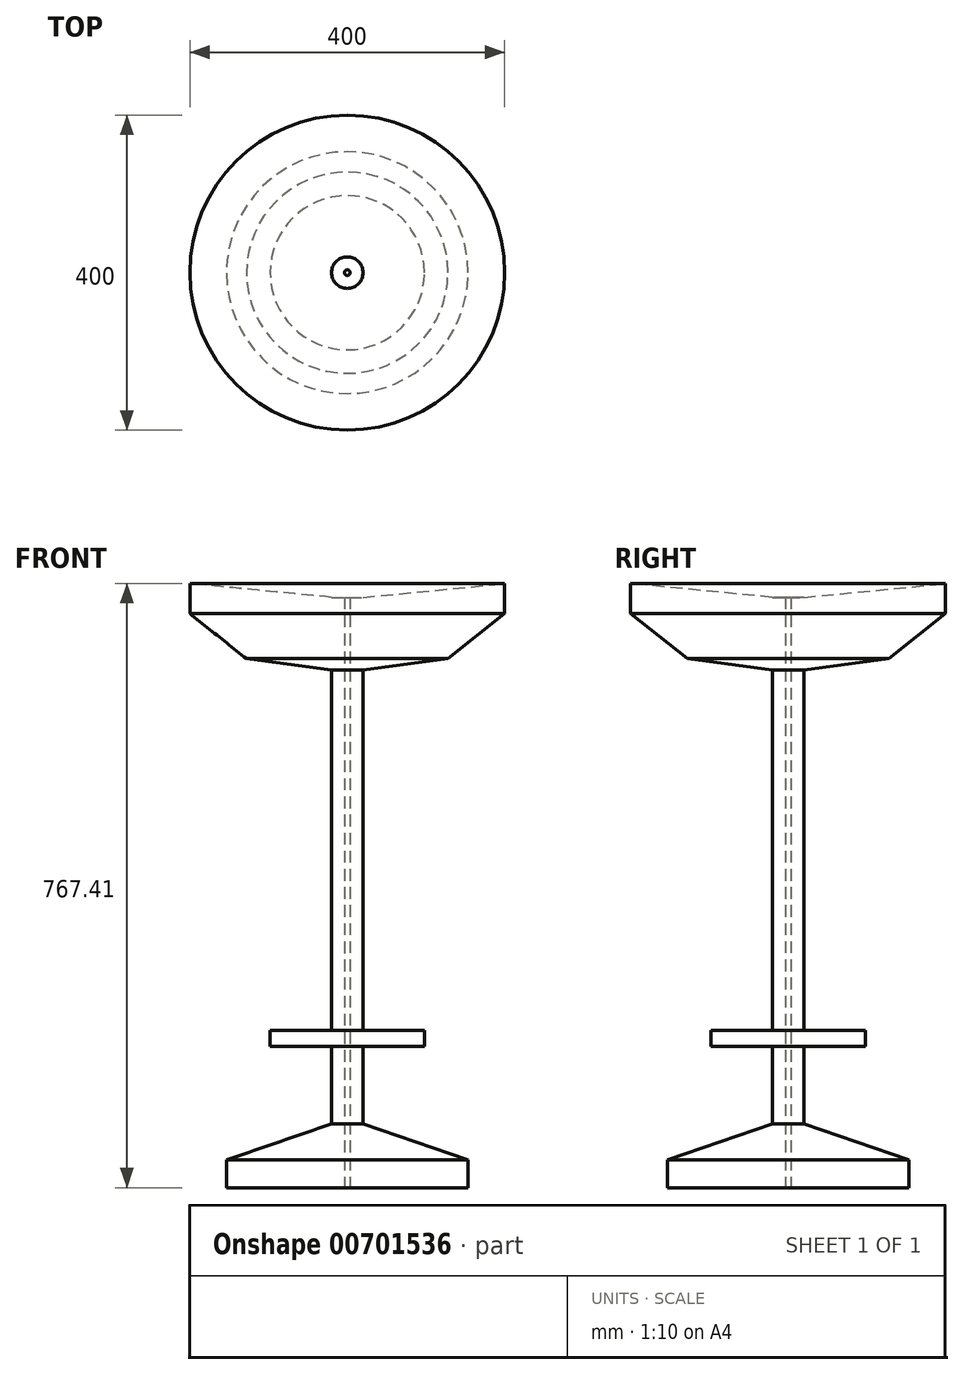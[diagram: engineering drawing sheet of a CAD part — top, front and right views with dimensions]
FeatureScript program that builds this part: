
annotation { "Feature Type Name" : "Feature", "Feature Type Description" : "" }
export const myFeature = defineFeature(function(context is Context, id is Id, definition is map)
    precondition{}
    {
        {
            var Q0;
            Q0=qCreatedBy(makeId("Front.planeOp"),FACE);
            var sketch = newSketch(context, id + "F0", { "sketchPlane" : qUnion([Q0])});
            skLineSegment(sketch, "E0", {"start": v(-3.54, 0) * mm, "end": v(-153.54, 0) * mm});
            skLineSegment(sketch, "E1", {"start": v(-153.54, 0) * mm, "end": v(-153.54, 35.15) * mm});
            skLineSegment(sketch, "E2", {"start": v(-153.54, 35.15) * mm, "end": v(-20, 80.98) * mm});
            skLineSegment(sketch, "E3", {"start": v(-20, 80.98) * mm, "end": v(-20, 179.55) * mm});
            skLineSegment(sketch, "E4", {"start": v(-20, 179.55) * mm, "end": v(-97.98, 179.55) * mm});
            skLineSegment(sketch, "E5", {"start": v(-97.98, 179.55) * mm, "end": v(-97.98, 199.66) * mm});
            skLineSegment(sketch, "E6", {"start": v(-97.98, 199.66) * mm, "end": v(-20, 199.66) * mm});
            skLineSegment(sketch, "E7", {"start": v(-20, 199.66) * mm, "end": v(-20, 657.55) * mm});
            skLineSegment(sketch, "E8", {"start": v(-20, 657.55) * mm, "end": v(-127.91, 671.94) * mm});
            skLineSegment(sketch, "E9", {"start": v(-127.91, 671.94) * mm, "end": v(-200, 729.14) * mm});
            skLineSegment(sketch, "E10", {"start": v(-200, 729.14) * mm, "end": v(-200, 767.4) * mm});
            skLineSegment(sketch, "E11", {"start": v(-200, 767.4) * mm, "end": v(-20, 749.9) * mm});
            skLineSegment(sketch, "E12", {"start": v(-20, 749.9) * mm, "end": v(-3.54, 749.9) * mm});
            skLineSegment(sketch, "E13", {"start": v(-3.54, 749.9) * mm, "end": v(-3.54, 0) * mm});
            skSolve(sketch);
        }
        {
            var Q0;
            Q0=qCreatedBy(makeId("Front.planeOp"),FACE);
            var sketch = newSketch(context, id + "F1", { "sketchPlane" : qUnion([Q0])});
            skLineSegment(sketch, "E14", {"start": v(0, 0) * mm, "end": v(0, 277.8) * mm});
            skSolve(sketch);
        }
        {
            var Q0;
            Q0 = qSketchRegion(id + "F0", true);
            var Q1;
            Q1=sQuery(id+"F1.wireOp",EDGE,"E14");
            revolve(context, id + "F2", {"entities" : qUnion([Q0]), "axis" : qUnion([Q1]), "revolveType" : RevolveType.FULL});
        }
    });
